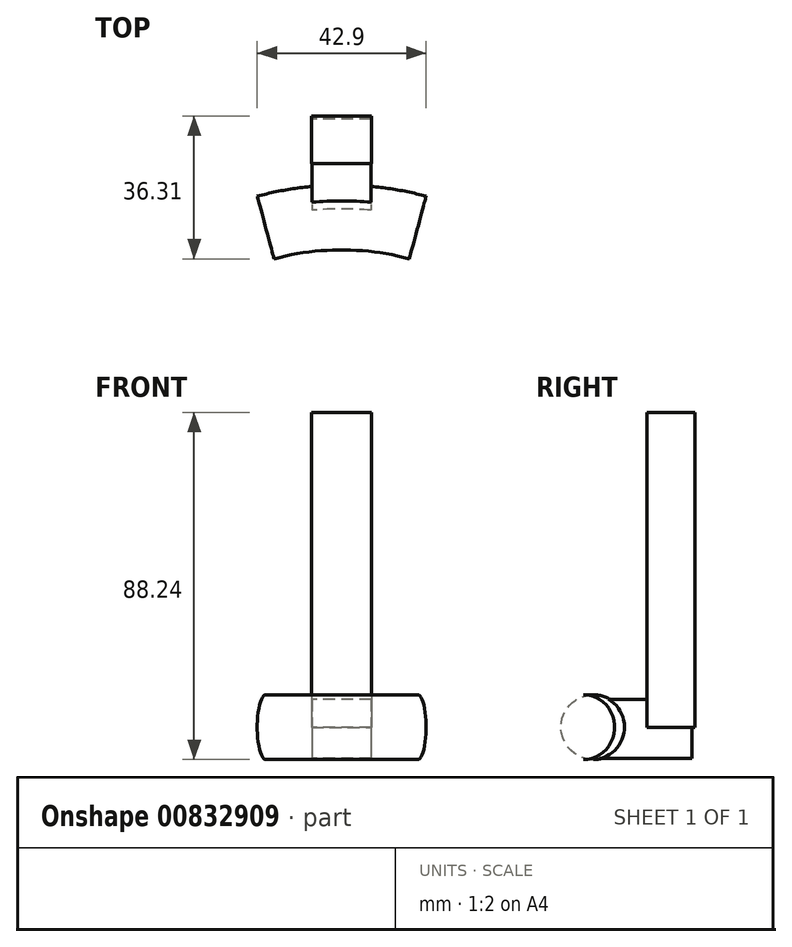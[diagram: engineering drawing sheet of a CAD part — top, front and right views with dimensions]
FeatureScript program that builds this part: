
annotation { "Feature Type Name" : "Feature", "Feature Type Description" : "" }
export const myFeature = defineFeature(function(context is Context, id is Id, definition is map)
    precondition{}
    {
        {
            var Q0;
            Q0=qCreatedBy(makeId("Right.planeOp"),FACE);
            var sketch = newSketch(context, id + "F0", { "sketchPlane" : qUnion([Q0])});
            skCircle(sketch, "E0", {"center": v(0, 0) * mm, "radius": 8.24 * mm});
            skLineSegment(sketch, "E1", {"start": v(-74.63, 11.66) * mm, "end": v(-74.63, -20.1) * mm});
            skSolve(sketch);
        }
        {
            var Q0;
            Q0=makeQuery(id+"F0.imprint","IMPRINT",FACE,{"disambiguationData":[TD([[makeQuery(id+"F0.imprint","IMPRINT",EDGE,{"derivedFrom":sQuery(id+"F0.wireOp",EDGE,"E0")}),1.0]])]});
            var Q1;
            Q1=sQuery(id+"F0.wireOp",EDGE,"E1");
            revolve(context, id + "F1", {"surfaceOperationType" : NewSurfaceOperationType.NEW, "entities" : qUnion([Q0]), "axis" : qUnion([Q1]), "revolveType" : RevolveType.SYMMETRIC, "angle" : 30 * degree});
        }
        {
            var Q0;
            Q0=qCreatedBy(makeId("Front.planeOp"),FACE);
            var sketch = newSketch(context, id + "F2", { "sketchPlane" : qUnion([Q0])});
            skLineSegment(sketch, "E2.bottom", {"start": v(7.5, 7.06) * mm, "end": v(-7.5, 7.06) * mm});
            skLineSegment(sketch, "E2.top", {"start": v(7.5, -7.94) * mm, "end": v(-7.5, -7.94) * mm});
            skLineSegment(sketch, "E2.left", {"start": v(7.5, 7.06) * mm, "end": v(7.5, -7.94) * mm});
            skLineSegment(sketch, "E2.right", {"start": v(-7.5, 7.06) * mm, "end": v(-7.5, -7.94) * mm});
            skSolve(sketch);
        }
        {
            var Q0;
            Q0 = qSketchRegion(id + "F2", true);
            extrude(context, id + "F3", {"entities" : qUnion([Q0]), "operationType" : NewBodyOperationType.ADD, "oppositeDirection" : true, "depth" : 25 * mm, "offsetDistance" : 25 * mm});
        }
        {
            var Q0;
            Q0=qCreatedBy(makeId("Top.planeOp"),FACE);
            var sketch = newSketch(context, id + "F4", { "sketchPlane" : qUnion([Q0])});
            skLineSegment(sketch, "E3.bottom", {"start": v(-7.67, 13.66) * mm, "end": v(7.52, 13.66) * mm});
            skLineSegment(sketch, "E3.top", {"start": v(-7.67, 25.8) * mm, "end": v(7.52, 25.8) * mm});
            skLineSegment(sketch, "E3.left", {"start": v(-7.67, 13.66) * mm, "end": v(-7.67, 25.8) * mm});
            skLineSegment(sketch, "E3.right", {"start": v(7.52, 13.66) * mm, "end": v(7.52, 25.8) * mm});
            skSolve(sketch);
        }
        {
            var Q0;
            Q0 = qSketchRegion(id + "F4", true);
            extrude(context, id + "F5", {"entities" : qUnion([Q0]), "operationType" : NewBodyOperationType.ADD, "depth" : 80 * mm, "offsetDistance" : 25 * mm});
        }
    });
